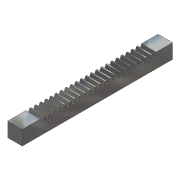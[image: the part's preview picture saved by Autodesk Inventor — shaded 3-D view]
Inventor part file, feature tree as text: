
AUTODESK INVENTOR PART (.ipt)
format: ipt  version: unknown  size: 359,424 bytes
history: native  units: mm (DEFAULTED — no unit token found)
features: extrude x3, sketch x3, projected_geometry x2
ambient origin geometry x8: Origin, YZ Plane, XZ Plane, XY Plane, X Axis, Y Axis, Z Axis, Center Point
feature tree (8):
  extrude  "Extrusion1"  Depth=19.05mm
  extrude  "Extrusion2"  Depth=2.11582mm
  extrude  "Extrusion3"  Depth=3.490659mm
  sketch  "Sketch1"  dims[d0=19.05mm d1=19.05mm]
  sketch  "Sketch2"  dims[d2=196.85mm d3=0.0mm d5=2.11582mm]
  projected_geometry  "Projected Loop1"
  sketch  "Sketch5"  dims[d6=3.490659mm d7=3.490659mm d11=6.64972mm d12=3.32486mm d13=3.32486mm d14=3.32486mm d15=23.7998mm d16=2.44856mm d17=210.0mm d19=6.6548mm d20=10.0mm d22=25.4mm d24=25.4mm d25=0.0mm d26=1.5494mm d27=1.905mm d28=25.4mm d29=0.0mm]
  projected_geometry  "Projected Loop4"
